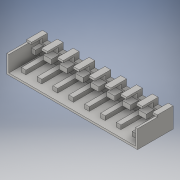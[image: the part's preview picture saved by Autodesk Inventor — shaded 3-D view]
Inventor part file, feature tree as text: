
AUTODESK INVENTOR PART (.ipt)
format: ipt  version: 2016 (Build 200138000, 138)  size: 391,680 bytes
history: native  units: in
note: dims shown in document units (in); Inventor stores cm internally (conversion verified against a paired STEP export)
features: projected_geometry x11, sketch x7, extrude x6
ambient origin geometry x8: Origin, YZ Plane, XZ Plane, XY Plane, X Axis, Y Axis, Z Axis, Center Point
bodies: Solid1 (feature_tree)
feature tree (24):
  extrude  "Extrusion1"  Depth=0.8in
  extrude  "Extrusion2"  Depth=0.23in
  sketch  "Sketch3"  dims[d4=0.25in d5=0.0in d8=0.3937in]
  extrude  "Extrusion3"  Depth=0.3937in
  extrude  "Extrusion4"  Depth=3.1496in
  extrude  "Extrusion5"  Depth=0.1in
  extrude  "Extrusion6"  Depth=0.9843in TaperAngle=0.0deg
  sketch  "Sketch1"  dims[d0=6.2992in d1=0.8in]
  sketch  "Sketch2"  dims[d2=0.4in d3=0.23in]
  sketch  "Sketch4"  dims[d9=1.5748in d11=360.0deg d13=3.1496in d15=0.7874in d16=0.3937in d18=1.0in]
  projected_geometry  "Projected Loop1"
  sketch  "Sketch5"  dims[d20=0.3937in d21=0.0in d22=0.1in]
  projected_geometry  "Projected Loop2"
  sketch  "Sketch6"  dims[d23=0.7874in d24=0.0in d25=0.9843in d26=0.0in]
  projected_geometry  "Projected Loop3"
  projected_geometry  "Projected Loop4"
  projected_geometry  "Projected Loop5"
  projected_geometry  "Projected Loop6"
  projected_geometry  "Projected Loop7"
  projected_geometry  "Projected Loop8"
  projected_geometry  "Projected Loop9"
  projected_geometry  "Projected Loop10"
  sketch  "Sketch7"  dims[d27=0.7874in d28=0.0in d29=0.25in d30=0.5in d31=3.1496in d33=0.7874in d34=0.3937in d36=1.0in d38=3.0in d39=0.0in]
  projected_geometry  "Projected Loop11"
